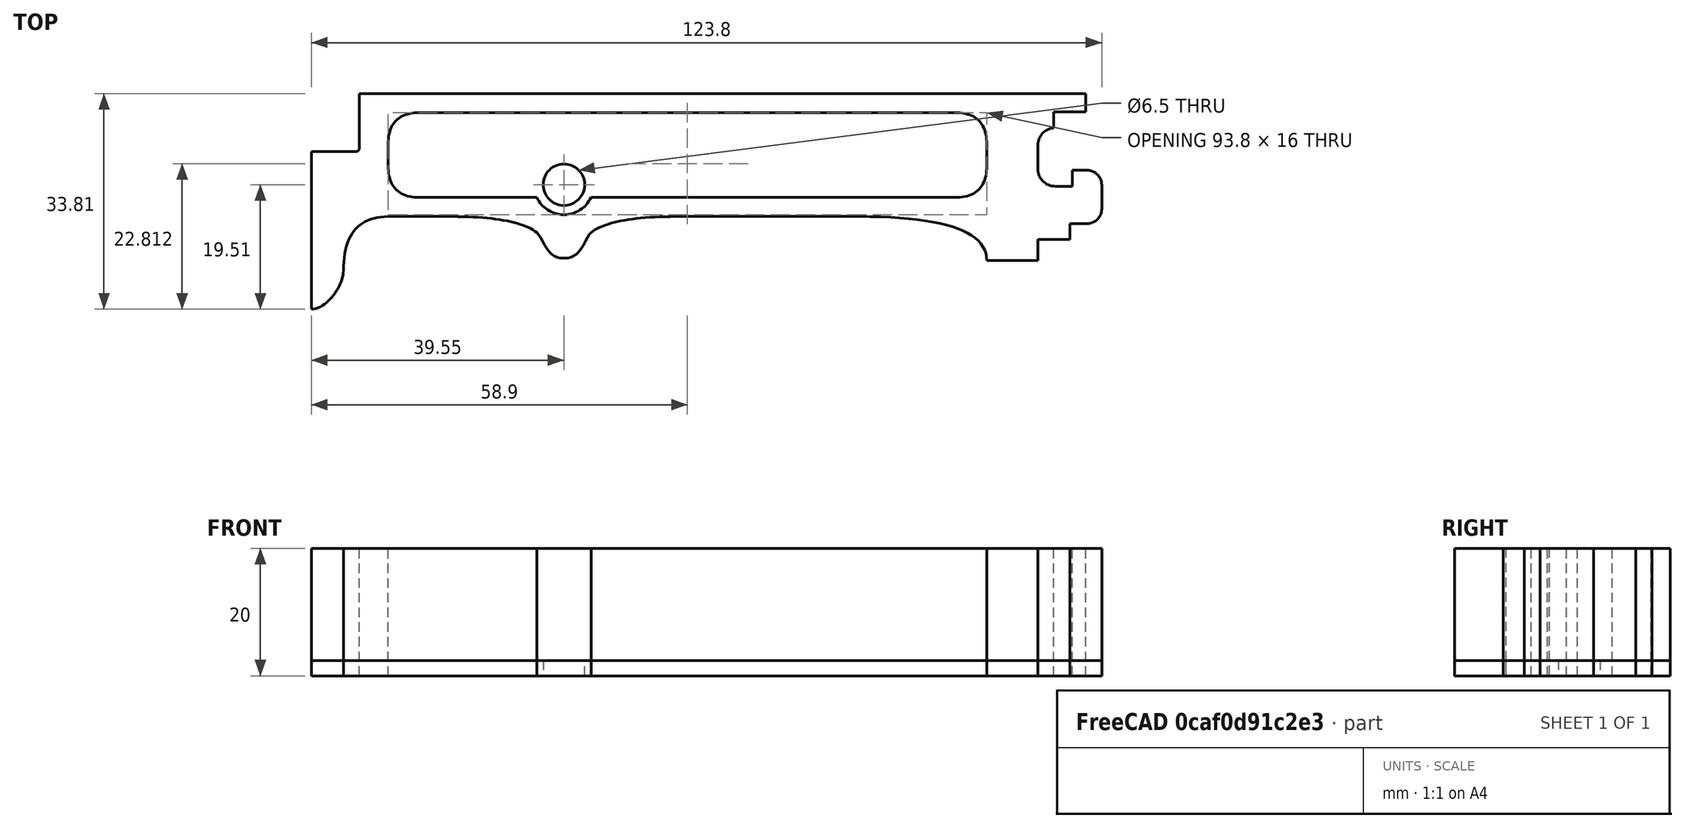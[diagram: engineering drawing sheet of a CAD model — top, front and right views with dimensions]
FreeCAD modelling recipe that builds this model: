
FCSTD DOCUMENT  (FreeCAD 0.19R0.19.2)
Label: v0_15
License: All rights reserved
LicenseURL: http://en.wikipedia.org/wiki/All_rights_reserved
objects: Sketcher::SketchObject×2, Part::Extrusion×2
note: 4 computed .brp shape members not serialized (recipe doc carries the construction recipe); baked Part::Feature solids carry a one-line shape summary decoded from their .brp

FEATURE [Sketcher::SketchObject] Sketch
  FullyConstrained = true
  sketch-geometry (69):
    g0: ArcOfCircle CenterX=-20 CenterY=-14.35 CenterZ=0 NormalX=0 NormalY=0 NormalZ=1 AngleXU=0 Radius=2.3 StartAngle=8e-16 EndAngle=1.5708
    g1: ArcOfCircle CenterX=-20 CenterY=-18.1 CenterZ=0 NormalX=0 NormalY=0 NormalZ=1 AngleXU=0 Radius=2.3 StartAngle=4.71239 EndAngle=6.28319
    g2: LineSegment StartX=-20 StartY=-20.4 StartZ=0 EndX=-22.7 EndY=-20.4 EndZ=0
    g3: LineSegment StartX=-22.7 StartY=-22.9 StartZ=0 EndX=-22.7 EndY=-20.4 EndZ=0
    g4: LineSegment StartX=-17.7 StartY=-14.35 StartZ=0 EndX=-17.7 EndY=-18.1 EndZ=0
    g5: LineSegment StartX=-25.2 StartY=-5.40742 StartZ=0 EndX=-25.2 EndY=-2.9 EndZ=0
    g6: LineSegment StartX=-25.2 StartY=-2.9 StartZ=0 EndX=-20.2 EndY=-2.9 EndZ=0
    g7: LineSegment StartX=-20.2 StartY=-2.9 StartZ=0 EndX=-20.2 EndY=0 EndZ=0
    g8: ArcOfCircle CenterX=-25 CenterY=-8.1 CenterZ=0 NormalX=0 NormalY=0 NormalZ=1 AngleXU=0 Radius=2.7 StartAngle=1.64494 EndAngle=3.14159
    g9: ArcOfCircle CenterX=-25 CenterY=-11.85 CenterZ=0 NormalX=0 NormalY=0 NormalZ=1 AngleXU=0 Radius=2.7 StartAngle=3.14159 EndAngle=4.71239
    g10: LineSegment StartX=-27.7 StartY=-8.1 StartZ=0 EndX=-27.7 EndY=-11.85 EndZ=0
    g11: LineSegment StartX=-25 StartY=-14.55 StartZ=0 EndX=-22.3 EndY=-14.55 EndZ=0
    g12: LineSegment StartX=-22.3 StartY=-12.05 StartZ=0 EndX=-22.3 EndY=-14.55 EndZ=0
    g13: LineSegment StartX=-22.3 StartY=-12.05 StartZ=0 EndX=-20 EndY=-12.05 EndZ=0
    g14: LineSegment StartX=-27.7 StartY=-22.9 StartZ=0 EndX=-22.7 EndY=-22.9 EndZ=0
    g15: LineSegment StartX=-27.7 StartY=-22.9 StartZ=0 EndX=-27.7 EndY=-26.2 EndZ=0
    g16: Circle CenterX=-101.95 CenterY=-14.3 CenterZ=0 NormalX=0 NormalY=0 NormalZ=1 AngleXU=0 Radius=3.25
    g17: LineSegment StartX=-134 StartY=0 StartZ=0 EndX=-20.2 EndY=0 EndZ=0
    g18: LineSegment StartX=-134 StartY=2.68e-14 StartZ=0 EndX=-134 EndY=-8.6 EndZ=0
    g19: LineSegment StartX=-134.5 StartY=-9.1 StartZ=0 EndX=-141.5 EndY=-9.1 EndZ=0
    g20: ArcOfCircle CenterX=-134.5 CenterY=-8.6 CenterZ=0 NormalX=0 NormalY=0 NormalZ=1 AngleXU=0 Radius=0.5 StartAngle=4.71239 EndAngle=6.28319
    g21: Circle CenterX=-97.7 CenterY=-21.8 CenterZ=0 NormalX=0 NormalY=0 NormalZ=1 AngleXU=0 Radius=1
    g22: Circle CenterX=-94.45 CenterY=-19.3 CenterZ=0 NormalX=0 NormalY=0 NormalZ=1 AngleXU=0 Radius=1
    g23: Circle CenterX=-84.45 CenterY=-19.3 CenterZ=0 NormalX=0 NormalY=0 NormalZ=1 AngleXU=0 Radius=1
    g24: BSplineCurve PolesCount=3 KnotsCount=2 Degree=2 IsPeriodic=0
    g25: GeomPoint X=-97.7 Y=-21.8 Z=0
    g26: GeomPoint X=-84.45 Y=-19.3 Z=0
    g27: Circle CenterX=-106.2 CenterY=-21.8 CenterZ=0 NormalX=0 NormalY=0 NormalZ=1 AngleXU=0 Radius=1
    g28: Circle CenterX=-109.45 CenterY=-19.3 CenterZ=0 NormalX=0 NormalY=0 NormalZ=1 AngleXU=0 Radius=1
    g29: Circle CenterX=-119.45 CenterY=-19.3 CenterZ=0 NormalX=0 NormalY=0 NormalZ=1 AngleXU=0 Radius=1
    g30: BSplineCurve PolesCount=3 KnotsCount=2 Degree=2 IsPeriodic=0
    g31: GeomPoint X=-106.2 Y=-21.8 Z=0
    g32: GeomPoint X=-119.45 Y=-19.3 Z=0
    g33: LineSegment StartX=-141.5 StartY=-9.1 StartZ=0 EndX=-141.5 EndY=-33.8 EndZ=0
    g34-g37: Circle x4 (B-spline internal-alignment scaffolding for g38; pole/knot coordinates omitted)
    g38: BSplineCurve PolesCount=4 KnotsCount=2 Degree=3 IsPeriodic=0
    g39: GeomPoint X=-141.5 Y=-33.8 Z=0
    g40: GeomPoint X=-136.5 Y=-27.8 Z=0
    g41: Circle CenterX=-136.5 CenterY=-27.8 CenterZ=0 NormalX=0 NormalY=0 NormalZ=1 AngleXU=0 Radius=1
    g42: Circle CenterX=-136.5 CenterY=-19.3 CenterZ=0 NormalX=0 NormalY=0 NormalZ=1 AngleXU=0 Radius=1
    g43: Circle CenterX=-129.5 CenterY=-19.3 CenterZ=0 NormalX=0 NormalY=0 NormalZ=1 AngleXU=0 Radius=1
    g44: BSplineCurve PolesCount=3 KnotsCount=2 Degree=2 IsPeriodic=0
    g45: GeomPoint X=-136.5 Y=-27.8 Z=0
    g46: GeomPoint X=-129.5 Y=-19.3 Z=0
    g47: LineSegment StartX=-129.5 StartY=-19.3 StartZ=0 EndX=-119.45 EndY=-19.3 EndZ=0
    g48: LineSegment StartX=-35.7 StartY=-26.2 StartZ=0 EndX=-27.7 EndY=-26.2 EndZ=0
    g49: Circle CenterX=-35.7 CenterY=-26.2 CenterZ=0 NormalX=0 NormalY=0 NormalZ=1 AngleXU=0 Radius=1
    g50: Circle CenterX=-35.7 CenterY=-19.3 CenterZ=0 NormalX=0 NormalY=0 NormalZ=1 AngleXU=0 Radius=1
    g51: Circle CenterX=-55.7 CenterY=-19.3 CenterZ=0 NormalX=0 NormalY=0 NormalZ=1 AngleXU=0 Radius=1
    g52: BSplineCurve PolesCount=3 KnotsCount=2 Degree=2 IsPeriodic=0
    g53: GeomPoint X=-35.7 Y=-26.2 Z=0
    g54: GeomPoint X=-55.7 Y=-19.3 Z=0
    g55: LineSegment StartX=-84.45 StartY=-19.3 StartZ=0 EndX=-55.7 EndY=-19.3 EndZ=0
    g56-g62: Circle x7 (B-spline internal-alignment scaffolding for g63; pole/knot coordinates omitted)
    g63: BSplineCurve PolesCount=7 KnotsCount=5 Degree=3 IsPeriodic=0
    g64-g68: GeomPoint x5 (B-spline internal-alignment scaffolding for g63; pole/knot coordinates omitted)
  constraints (111):
    c: Block(g1)
    c: Block(g0)
    c: Coincident(g2,g1)
    c: Horizontal(g2)
    c: Vertical(g3)
    c: Coincident(g3,g2)
    c: Coincident(g4,g0)
    c: Coincident(g4,g1)
    c: Vertical(g4)
    c: Vertical(g5)
    c: Block(g5)
    c: Coincident(g6,g5)
    c: Horizontal(g6)
    c: Vertical(g7)
    c: Block(g7)
    c: Block(g6)
    c: Coincident(g8,g5)
    c: Block(g9)
    c: Coincident(g10,g8)
    c: Coincident(g10,g9)
    c: Vertical(g10)
    c: Block(g10)
    c: Coincident(g11,g9)
    c: Horizontal(g11)
    c: Vertical(g12)
    c: Coincident(g12,g11)
    c: Block(g12)
    c: Coincident(g13,g0)
    c: Horizontal(g13)
    c: Block(g13)
    c: Coincident(g14,g3)
    c: Horizontal(g14)
    c: Block(g14)
    c: Coincident(g15,g14)
    c: Vertical(g15)
    c: Block(g16)
    c: Coincident(g17,g7)
    c: Horizontal(g17)
    c: Vertical(g18)
    c: Distance(g18) = 8.6
    c: Horizontal(g19)
    c: Distance(g19) = 7
    c: Coincident(g20,g18)
    c: Coincident(g20,g19)
    c: Block(g20)
    c: Block(g17)
    c: Weight(g21) = 1
    c: Equal(g21,g22)
    c: Equal(g21,g23)
    c: InternalAlignment(g21,g24)
    c: InternalAlignment(g22,g24)
    c: InternalAlignment(g23,g24)
    c: InternalAlignment(g25,g24)
    c: InternalAlignment(g26,g24)
    c: Weight(g27) = 1
    c: Equal(g27,g28)
    c: Equal(g27,g29)
    c: InternalAlignment(g27,g30)
    c: InternalAlignment(g28,g30)
    c: InternalAlignment(g29,g30)
    c: InternalAlignment(g31,g30)
    c: InternalAlignment(g32,g30)
    c: Block(g30)
    c: Block(g24)
    c: Coincident(g33,g19)
    c: Vertical(g33)
    c: Block(g33)
    c: Coincident(g38,g33)
    c: Weight(g34) = 1
    c: Equal(g34,g35)
    c: Equal(g34,g36)
    c: Equal(g34,g37)
    c: InternalAlignment(g34-g37 -> g38) x4
    c: InternalAlignment(g39,g38)
    c: InternalAlignment(g40,g38)
    c: Weight(g41) = 1
    c: Equal(g41,g42)
    c: Equal(g41,g43)
    c: InternalAlignment(g41,g44)
    c: InternalAlignment(g42,g44)
    c: InternalAlignment(g43,g44)
    c: InternalAlignment(g45,g44)
    c: InternalAlignment(g46,g44)
    c: Block(g38)
    c: Block(g44)
    c: Coincident(g47,g44)
    c: Coincident(g47,g30)
    c: Horizontal(g47)
    c: Horizontal(g48)
    c: Distance(g48) = 8
    c: Block(g48)
    c: Block(g15)
    c: Block(g8)
    c: Coincident(g52,g48)
    c: Weight(g49) = 1
    c: Equal(g49,g50)
    c: Equal(g49,g51)
    c: InternalAlignment(g49,g52)
    c: InternalAlignment(g50,g52)
    c: InternalAlignment(g51,g52)
    c: InternalAlignment(g53,g52)
    c: InternalAlignment(g54,g52)
    c: Block(g52)
    c: Coincident(g55,g24)
    c: Coincident(g55,g52)
    c: Horizontal(g55)
    c: Weight(g56) = 1
    c: Equal(g56, g57-g62) x6
    c: InternalAlignment(g56-g62 -> g63) x7
    c: InternalAlignment(g64-g68 -> g63) x5
    c: Block(g63)
FEATURE [Part::Extrusion] Extrude
  Base = -> Sketch
  Dir = (0,0,1)
  DirMode = 2
  FaceMakerClass = Part::FaceMakerBullseye
  LengthFwd = 2.4
  LengthRev = 0
  Solid = true
  Symmetric = false
FEATURE [Sketcher::SketchObject] Sketch001
  FullyConstrained = true
  sketch-geometry (98):
    g0: ArcOfCircle CenterX=-20 CenterY=-14.35 CenterZ=0 NormalX=0 NormalY=0 NormalZ=1 AngleXU=0 Radius=2.3 StartAngle=8e-16 EndAngle=1.5708
    g1: ArcOfCircle CenterX=-20 CenterY=-18.1 CenterZ=0 NormalX=0 NormalY=0 NormalZ=1 AngleXU=0 Radius=2.3 StartAngle=4.71239 EndAngle=6.28319
    g2: LineSegment StartX=-20 StartY=-20.4 StartZ=0 EndX=-22.7 EndY=-20.4 EndZ=0
    g3: LineSegment StartX=-22.7 StartY=-22.9 StartZ=0 EndX=-22.7 EndY=-20.4 EndZ=0
    g4: LineSegment StartX=-17.7 StartY=-14.35 StartZ=0 EndX=-17.7 EndY=-18.1 EndZ=0
    g5: LineSegment StartX=-25.2 StartY=-5.40742 StartZ=0 EndX=-25.2 EndY=-2.9 EndZ=0
    g6: LineSegment StartX=-25.2 StartY=-2.9 StartZ=0 EndX=-20.2 EndY=-2.9 EndZ=0
    g7: LineSegment StartX=-20.2 StartY=-2.9 StartZ=0 EndX=-20.2 EndY=0 EndZ=0
    g8: ArcOfCircle CenterX=-25 CenterY=-8.1 CenterZ=0 NormalX=0 NormalY=0 NormalZ=1 AngleXU=0 Radius=2.7 StartAngle=1.64494 EndAngle=3.14159
    g9: ArcOfCircle CenterX=-25 CenterY=-11.85 CenterZ=0 NormalX=0 NormalY=0 NormalZ=1 AngleXU=0 Radius=2.7 StartAngle=3.14159 EndAngle=4.71239
    g10: LineSegment StartX=-27.7 StartY=-8.1 StartZ=0 EndX=-27.7 EndY=-11.85 EndZ=0
    g11: LineSegment StartX=-25 StartY=-14.55 StartZ=0 EndX=-22.3 EndY=-14.55 EndZ=0
    g12: LineSegment StartX=-22.3 StartY=-12.05 StartZ=0 EndX=-22.3 EndY=-14.55 EndZ=0
    g13: LineSegment StartX=-22.3 StartY=-12.05 StartZ=0 EndX=-20 EndY=-12.05 EndZ=0
    g14: LineSegment StartX=-27.7 StartY=-22.9 StartZ=0 EndX=-22.7 EndY=-22.9 EndZ=0
    g15: LineSegment StartX=-27.7 StartY=-22.9 StartZ=0 EndX=-27.7 EndY=-26.2 EndZ=0
    g16: LineSegment StartX=-134 StartY=0 StartZ=0 EndX=-134 EndY=-8.6 EndZ=0
    g17: LineSegment StartX=-134.5 StartY=-9.1 StartZ=0 EndX=-141.5 EndY=-9.1 EndZ=0
    g18: ArcOfCircle CenterX=-134.5 CenterY=-8.6 CenterZ=0 NormalX=0 NormalY=0 NormalZ=1 AngleXU=0 Radius=0.5 StartAngle=4.71239 EndAngle=6.28319
    g19: Circle CenterX=-97.7 CenterY=-21.8 CenterZ=0 NormalX=0 NormalY=0 NormalZ=1 AngleXU=0 Radius=1
    g20: Circle CenterX=-94.45 CenterY=-19.3 CenterZ=0 NormalX=0 NormalY=0 NormalZ=1 AngleXU=0 Radius=1
    g21: Circle CenterX=-84.45 CenterY=-19.3 CenterZ=0 NormalX=0 NormalY=0 NormalZ=1 AngleXU=0 Radius=1
    g22: BSplineCurve PolesCount=3 KnotsCount=2 Degree=2 IsPeriodic=0
    g23: GeomPoint X=-97.7 Y=-21.8 Z=0
    g24: GeomPoint X=-84.45 Y=-19.3 Z=0
    g25: Circle CenterX=-106.2 CenterY=-21.8 CenterZ=0 NormalX=0 NormalY=0 NormalZ=1 AngleXU=0 Radius=1
    g26: Circle CenterX=-109.45 CenterY=-19.3 CenterZ=0 NormalX=0 NormalY=0 NormalZ=1 AngleXU=0 Radius=1
    g27: Circle CenterX=-119.45 CenterY=-19.3 CenterZ=0 NormalX=0 NormalY=0 NormalZ=1 AngleXU=0 Radius=1
    g28: BSplineCurve PolesCount=3 KnotsCount=2 Degree=2 IsPeriodic=0
    g29: GeomPoint X=-106.2 Y=-21.8 Z=0
    g30: GeomPoint X=-119.45 Y=-19.3 Z=0
    g31: LineSegment StartX=-141.5 StartY=-9.1 StartZ=0 EndX=-141.5 EndY=-33.8 EndZ=0
    g32-g35: Circle x4 (B-spline internal-alignment scaffolding for g36; pole/knot coordinates omitted)
    g36: BSplineCurve PolesCount=4 KnotsCount=2 Degree=3 IsPeriodic=0
    g37: GeomPoint X=-141.5 Y=-33.8 Z=0
    g38: GeomPoint X=-136.5 Y=-27.8 Z=0
    g39: Circle CenterX=-136.5 CenterY=-27.8 CenterZ=0 NormalX=0 NormalY=0 NormalZ=1 AngleXU=0 Radius=1
    g40: Circle CenterX=-136.5 CenterY=-19.3 CenterZ=0 NormalX=0 NormalY=0 NormalZ=1 AngleXU=0 Radius=1
    g41: Circle CenterX=-129.5 CenterY=-19.3 CenterZ=0 NormalX=0 NormalY=0 NormalZ=1 AngleXU=0 Radius=1
    g42: BSplineCurve PolesCount=3 KnotsCount=2 Degree=2 IsPeriodic=0
    g43: GeomPoint X=-136.5 Y=-27.8 Z=0
    g44: GeomPoint X=-129.5 Y=-19.3 Z=0
    g45: LineSegment StartX=-129.5 StartY=-19.3 StartZ=0 EndX=-119.45 EndY=-19.3 EndZ=0
    g46: LineSegment StartX=-35.7 StartY=-26.2 StartZ=0 EndX=-27.7 EndY=-26.2 EndZ=0
    g47: Circle CenterX=-35.7 CenterY=-26.2 CenterZ=0 NormalX=0 NormalY=0 NormalZ=1 AngleXU=0 Radius=1
    g48: Circle CenterX=-35.7 CenterY=-19.3 CenterZ=0 NormalX=0 NormalY=0 NormalZ=1 AngleXU=0 Radius=1
    g49: Circle CenterX=-55.7 CenterY=-19.3 CenterZ=0 NormalX=0 NormalY=0 NormalZ=1 AngleXU=0 Radius=1
    g50: BSplineCurve PolesCount=3 KnotsCount=2 Degree=2 IsPeriodic=0
    g51: GeomPoint X=-35.7 Y=-26.2 Z=0
    g52: GeomPoint X=-55.7 Y=-19.3 Z=0
    g53: LineSegment StartX=-84.45 StartY=-19.3 StartZ=0 EndX=-55.7 EndY=-19.3 EndZ=0
    g54-g60: Circle x7 (B-spline internal-alignment scaffolding for g61; pole/knot coordinates omitted)
    g61: BSplineCurve PolesCount=7 KnotsCount=5 Degree=3 IsPeriodic=0
    g62-g66: GeomPoint x5 (B-spline internal-alignment scaffolding for g61; pole/knot coordinates omitted)
    g67: LineSegment StartX=-134 StartY=0 StartZ=0 EndX=-20.2 EndY=0 EndZ=0
    g68: ArcOfCircle CenterX=-101.95 CenterY=-14.3 CenterZ=0 NormalX=0 NormalY=0 NormalZ=1 AngleXU=0 Radius=4.69707 StartAngle=3.58144 EndAngle=5.84334
    g69: Circle CenterX=-40.7 CenterY=-3 CenterZ=0 NormalX=0 NormalY=0 NormalZ=1 AngleXU=0 Radius=1
    g70: Circle CenterX=-35.7 CenterY=-3 CenterZ=0 NormalX=0 NormalY=0 NormalZ=1 AngleXU=0 Radius=1
    g71: Circle CenterX=-35.7 CenterY=-8 CenterZ=0 NormalX=0 NormalY=0 NormalZ=1 AngleXU=0 Radius=1
    g72: BSplineCurve PolesCount=3 KnotsCount=2 Degree=2 IsPeriodic=0
    g73: GeomPoint X=-40.7 Y=-3 Z=0
    g74: GeomPoint X=-35.7 Y=-8 Z=0
    g75: Circle CenterX=-35.7 CenterY=-11.3 CenterZ=0 NormalX=0 NormalY=0 NormalZ=1 AngleXU=0 Radius=1
    g76: Circle CenterX=-35.7 CenterY=-16.3 CenterZ=0 NormalX=0 NormalY=0 NormalZ=1 AngleXU=0 Radius=1
    g77: Circle CenterX=-40.7 CenterY=-16.3 CenterZ=0 NormalX=0 NormalY=0 NormalZ=1 AngleXU=0 Radius=1
    g78: BSplineCurve PolesCount=3 KnotsCount=2 Degree=2 IsPeriodic=0
    g79: GeomPoint X=-35.7 Y=-11.3 Z=0
    g80: GeomPoint X=-40.7 Y=-16.3 Z=0
    g81: Circle CenterX=-124.5 CenterY=-16.3 CenterZ=0 NormalX=0 NormalY=0 NormalZ=1 AngleXU=0 Radius=1
    g82: Circle CenterX=-129.5 CenterY=-16.3 CenterZ=0 NormalX=0 NormalY=0 NormalZ=1 AngleXU=0 Radius=1
    g83: Circle CenterX=-129.5 CenterY=-11.3 CenterZ=0 NormalX=0 NormalY=0 NormalZ=1 AngleXU=0 Radius=1
    g84: BSplineCurve PolesCount=3 KnotsCount=2 Degree=2 IsPeriodic=0
    g85: GeomPoint X=-124.5 Y=-16.3 Z=0
    g86: GeomPoint X=-129.5 Y=-11.3 Z=0
    g87: Circle CenterX=-129.5 CenterY=-8 CenterZ=0 NormalX=0 NormalY=0 NormalZ=1 AngleXU=0 Radius=1
    g88: Circle CenterX=-129.5 CenterY=-3 CenterZ=0 NormalX=0 NormalY=0 NormalZ=1 AngleXU=0 Radius=1
    g89: Circle CenterX=-124.5 CenterY=-3 CenterZ=0 NormalX=0 NormalY=0 NormalZ=1 AngleXU=0 Radius=1
    g90: BSplineCurve PolesCount=3 KnotsCount=2 Degree=2 IsPeriodic=0
    g91: GeomPoint X=-129.5 Y=-8 Z=0
    g92: GeomPoint X=-124.5 Y=-3 Z=0
    g93: LineSegment StartX=-129.5 StartY=-8 StartZ=0 EndX=-129.5 EndY=-11.3 EndZ=0
    g94: LineSegment StartX=-124.5 StartY=-3 StartZ=0 EndX=-40.7 EndY=-3 EndZ=0
    g95: LineSegment StartX=-35.7 StartY=-8 StartZ=0 EndX=-35.7 EndY=-11.3 EndZ=0
    g96: LineSegment StartX=-40.7 StartY=-16.3 StartZ=0 EndX=-97.7 EndY=-16.3 EndZ=0
    g97: LineSegment StartX=-106.2 StartY=-16.3 StartZ=0 EndX=-124.5 EndY=-16.3 EndZ=0
  constraints (162):
    c: Block(g1)
    c: Block(g0)
    c: Coincident(g2,g1)
    c: Horizontal(g2)
    c: Vertical(g3)
    c: Coincident(g3,g2)
    c: Coincident(g4,g0)
    c: Coincident(g4,g1)
    c: Vertical(g4)
    c: Vertical(g5)
    c: Block(g5)
    c: Coincident(g6,g5)
    c: Horizontal(g6)
    c: Vertical(g7)
    c: Block(g7)
    c: Block(g6)
    c: Coincident(g8,g5)
    c: Block(g9)
    c: Coincident(g10,g8)
    c: Coincident(g10,g9)
    c: Vertical(g10)
    c: Block(g10)
    c: Coincident(g11,g9)
    c: Horizontal(g11)
    c: Vertical(g12)
    c: Coincident(g12,g11)
    c: Block(g12)
    c: Coincident(g13,g0)
    c: Horizontal(g13)
    c: Block(g13)
    c: Coincident(g14,g3)
    c: Horizontal(g14)
    c: Block(g14)
    c: Coincident(g15,g14)
    c: Vertical(g15)
    c: Vertical(g16)
    c: Distance(g16) = 8.6
    c: Horizontal(g17)
    c: Distance(g17) = 7
    c: Coincident(g18,g16)
    c: Coincident(g18,g17)
    c: Block(g18)
    c: Weight(g19) = 1
    c: Equal(g19,g20)
    c: Equal(g19,g21)
    c: InternalAlignment(g19,g22)
    c: InternalAlignment(g20,g22)
    c: InternalAlignment(g21,g22)
    c: InternalAlignment(g23,g22)
    c: InternalAlignment(g24,g22)
    c: Weight(g25) = 1
    c: Equal(g25,g26)
    c: Equal(g25,g27)
    c: InternalAlignment(g25,g28)
    c: InternalAlignment(g26,g28)
    c: InternalAlignment(g27,g28)
    c: InternalAlignment(g29,g28)
    c: InternalAlignment(g30,g28)
    c: Block(g22)
    c: Coincident(g31,g17)
    c: Vertical(g31)
    c: Block(g31)
    c: Coincident(g36,g31)
    c: Weight(g32) = 1
    c: Equal(g32,g33)
    c: Equal(g32,g34)
    c: Equal(g32,g35)
    c: InternalAlignment(g32-g35 -> g36) x4
    c: InternalAlignment(g37,g36)
    c: InternalAlignment(g38,g36)
    c: Weight(g39) = 1
    c: Equal(g39,g40)
    c: Equal(g39,g41)
    c: InternalAlignment(g39,g42)
    c: InternalAlignment(g40,g42)
    c: InternalAlignment(g41,g42)
    c: InternalAlignment(g43,g42)
    c: InternalAlignment(g44,g42)
    c: Block(g36)
    c: Coincident(g45,g42)
    c: Coincident(g45,g28)
    c: Horizontal(g45)
    c: Horizontal(g46)
    c: Distance(g46) = 8
    c: Block(g46)
    c: Block(g15)
    c: Block(g8)
    c: Coincident(g50,g46)
    c: Weight(g47) = 1
    c: Equal(g47,g48)
    c: Equal(g47,g49)
    c: InternalAlignment(g47,g50)
    c: InternalAlignment(g48,g50)
    c: InternalAlignment(g49,g50)
    c: InternalAlignment(g51,g50)
    c: InternalAlignment(g52,g50)
    c: Block(g50)
    c: Coincident(g53,g22)
    c: Coincident(g53,g50)
    c: Horizontal(g53)
    c: Weight(g54) = 1
    c: Equal(g54, g55-g60) x6
    c: InternalAlignment(g54-g60 -> g61) x7
    c: InternalAlignment(g62-g66 -> g61) x5
    c: Block(g61)
    c: Coincident(g67,g16)
    c: Coincident(g67,g7)
    c: Horizontal(g67)
    c: Block(g68)
    c: Block(g28)
    c: Block(g42)
    c: Weight(g69) = 1
    c: Equal(g69,g70)
    c: Equal(g69,g71)
    c: InternalAlignment(g69,g72)
    c: InternalAlignment(g70,g72)
    c: InternalAlignment(g71,g72)
    c: InternalAlignment(g73,g72)
    c: InternalAlignment(g74,g72)
    c: Weight(g75) = 1
    c: Equal(g75,g76)
    c: Equal(g75,g77)
    c: InternalAlignment(g75,g78)
    c: InternalAlignment(g76,g78)
    c: InternalAlignment(g77,g78)
    c: InternalAlignment(g79,g78)
    c: InternalAlignment(g80,g78)
    c: Weight(g81) = 1
    c: Equal(g81,g82)
    c: Equal(g81,g83)
    c: InternalAlignment(g81,g84)
    c: InternalAlignment(g82,g84)
    c: InternalAlignment(g83,g84)
    c: InternalAlignment(g85,g84)
    c: InternalAlignment(g86,g84)
    c: Weight(g87) = 1
    c: Equal(g87,g88)
    c: Equal(g87,g89)
    c: InternalAlignment(g87,g90)
    c: InternalAlignment(g88,g90)
    c: InternalAlignment(g89,g90)
    c: InternalAlignment(g91,g90)
    c: InternalAlignment(g92,g90)
    c: Block(g90)
    c: Block(g84)
    c: Block(g78)
    c: Block(g72)
    c: Coincident(g93,g90)
    c: Coincident(g93,g84)
    c: Vertical(g93)
    c: Coincident(g94,g90)
    c: Horizontal(g94)
    c: Coincident(g95,g72)
    c: Coincident(g95,g78)
    c: Vertical(g95)
    c: Coincident(g96,g78)
    c: Coincident(g96,g68)
    c: Horizontal(g96)
    c: Coincident(g97,g68)
    c: Coincident(g97,g84)
    c: Horizontal(g97)
    c: Block(g94)
FEATURE [Part::Extrusion] Extrude001
  Base = -> Sketch001
  Dir = (0,0,1)
  DirMode = 2
  FaceMakerClass = Part::FaceMakerBullseye
  LengthFwd = 20
  LengthRev = 0
  Solid = true
  Symmetric = false
